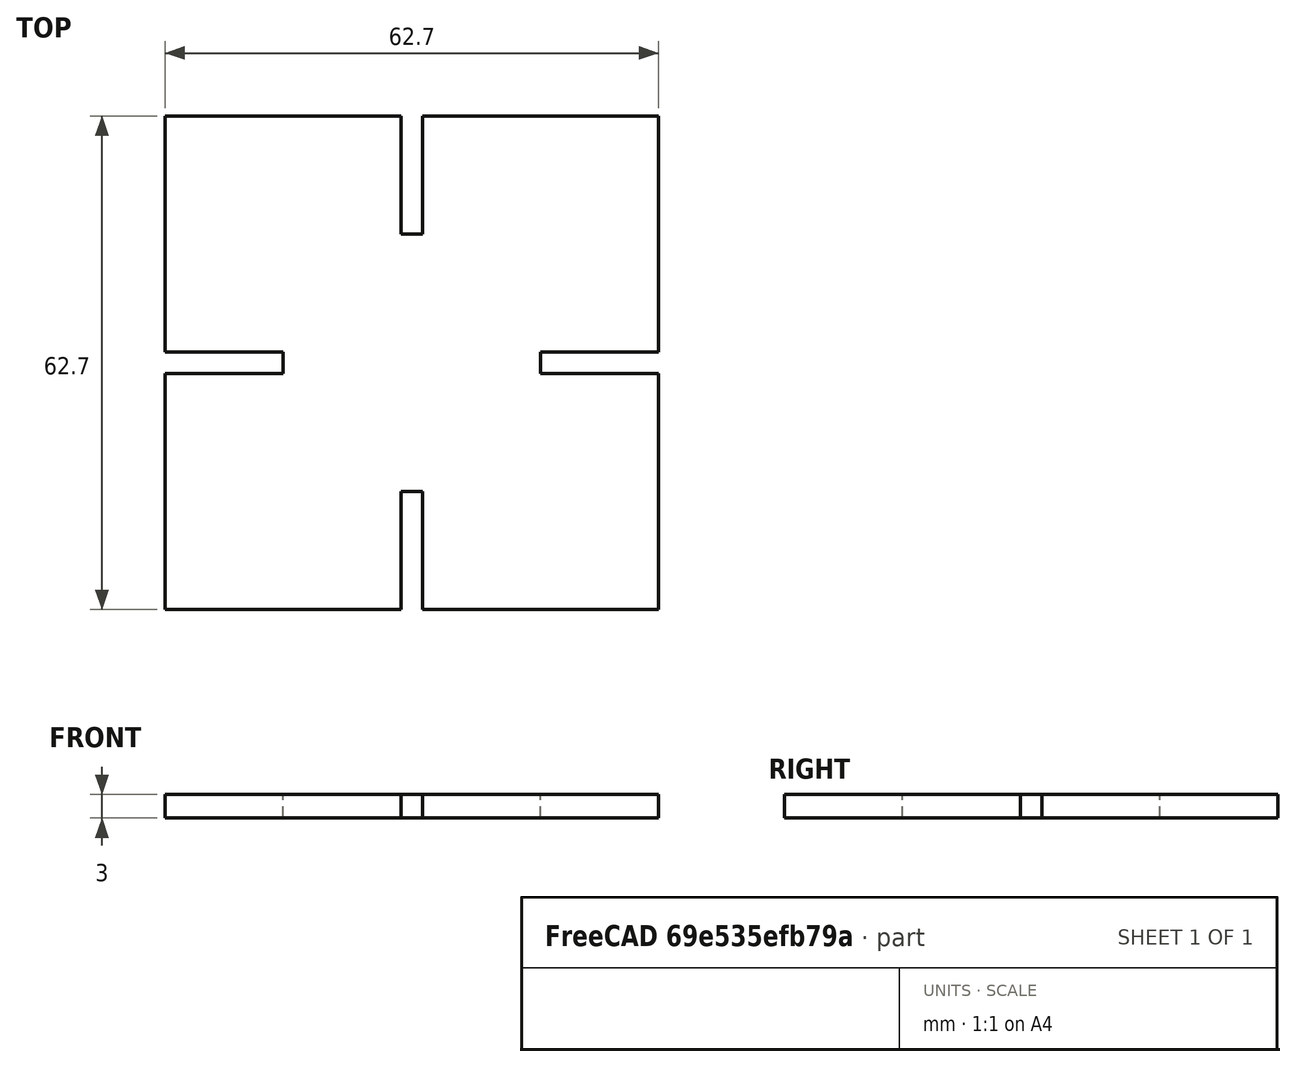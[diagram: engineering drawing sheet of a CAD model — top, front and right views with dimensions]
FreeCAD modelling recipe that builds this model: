
FCSTD DOCUMENT  (FreeCAD 0.19RUnknown)
Label: block
License: All rights reserved
LicenseURL: http://en.wikipedia.org/wiki/All_rights_reserved
objects: Sketcher::SketchObject×1, PartDesign::Pad×1, PartDesign::Body×1, Spreadsheet::Sheet×1, TechDraw::DrawSVGTemplate×1, TechDraw::DrawViewPart×1, TechDraw::DrawPage×1
note: 4 computed .brp shape members not serialized (recipe doc carries the construction recipe); baked Part::Feature solids carry a one-line shape summary decoded from their .brp

FEATURE [Sketcher::SketchObject] Sketch
  FullyConstrained = true
  MapMode = 5
  Support = -> [XY_Plane]
  expr: Constraints[43] = Spreadsheet.slotwidth
  sketch-geometry (20):
    g0: LineSegment StartX=1.35 StartY=31.35 StartZ=0 EndX=31.35 EndY=31.35 EndZ=0
    g1: LineSegment StartX=31.35 StartY=31.35 StartZ=0 EndX=31.35 EndY=1.35 EndZ=0
    g2: LineSegment StartX=31.35 StartY=1.35 StartZ=0 EndX=16.35 EndY=1.35 EndZ=0
    g3: LineSegment StartX=16.35 StartY=1.35 StartZ=0 EndX=16.35 EndY=-1.35 EndZ=0
    g4: LineSegment StartX=16.35 StartY=-1.35 StartZ=0 EndX=31.35 EndY=-1.35 EndZ=0
    g5: LineSegment StartX=31.35 StartY=-1.35 StartZ=0 EndX=31.35 EndY=-31.35 EndZ=0
    g6: LineSegment StartX=31.35 StartY=-31.35 StartZ=0 EndX=1.35 EndY=-31.35 EndZ=0
    g7: LineSegment StartX=1.35 StartY=-31.35 StartZ=0 EndX=1.35 EndY=-16.35 EndZ=0
    g8: LineSegment StartX=1.35 StartY=-16.35 StartZ=0 EndX=-1.35 EndY=-16.35 EndZ=0
    g9: LineSegment StartX=-1.35 StartY=-16.35 StartZ=0 EndX=-1.35 EndY=-31.35 EndZ=0
    g10: LineSegment StartX=-1.35 StartY=-31.35 StartZ=0 EndX=-31.35 EndY=-31.35 EndZ=0
    g11: LineSegment StartX=-31.35 StartY=-31.35 StartZ=0 EndX=-31.35 EndY=-1.35 EndZ=0
    g12: LineSegment StartX=-31.35 StartY=-1.35 StartZ=0 EndX=-16.35 EndY=-1.35 EndZ=0
    g13: LineSegment StartX=-16.35 StartY=-1.35 StartZ=0 EndX=-16.35 EndY=1.35 EndZ=0
    g14: LineSegment StartX=-16.35 StartY=1.35 StartZ=0 EndX=-31.35 EndY=1.35 EndZ=0
    g15: LineSegment StartX=-31.35 StartY=1.35 StartZ=0 EndX=-31.35 EndY=31.35 EndZ=0
    g16: LineSegment StartX=-31.35 StartY=31.35 StartZ=0 EndX=-1.35 EndY=31.35 EndZ=0
    g17: LineSegment StartX=-1.35 StartY=31.35 StartZ=0 EndX=-1.35 EndY=16.35 EndZ=0
    g18: LineSegment StartX=-1.35 StartY=16.35 StartZ=0 EndX=1.35 EndY=16.35 EndZ=0
    g19: LineSegment StartX=1.35 StartY=16.35 StartZ=0 EndX=1.35 EndY=31.35 EndZ=0
  constraints (59):
    c: Horizontal(g0)
    c: Coincident(g0,g1)
    c: Vertical(g1)
    c: Coincident(g1,g2)
    c: Horizontal(g2)
    c: Coincident(g2,g3)
    c: Vertical(g3)
    c: Coincident(g3,g4)
    c: Horizontal(g4)
    c: Coincident(g4,g5)
    c: Coincident(g5,g6)
    c: Coincident(g6,g7)
    c: Vertical(g7)
    c: Coincident(g7,g8)
    c: Coincident(g8,g9)
    c: Coincident(g9,g10)
    c: Horizontal(g10)
    c: Coincident(g10,g11)
    c: Vertical(g11)
    c: Coincident(g11,g12)
    c: Horizontal(g12)
    c: Coincident(g12,g13)
    c: Vertical(g13)
    c: Coincident(g13,g14)
    c: Horizontal(g14)
    c: Coincident(g14,g15)
    c: Vertical(g15)
    c: Coincident(g15,g16)
    c: Horizontal(g16)
    c: Coincident(g16,g17)
    c: Vertical(g17)
    c: Coincident(g17,g18)
    c: Horizontal(g18)
    c: Coincident(g18,g19)
    c: Vertical(g19)
    c: Coincident(g0,g19)
    c: Horizontal(g6)
    c: Horizontal(g8)
    c: Vertical(g9)
    c: Vertical(g5)
    c: Equal(g8,g3)
    c: Equal(g3,g18)
    c: Equal(g18,g13)
    c: Distance(g13) = 2.7
    c: Equal(g16,g15)
    c: Equal(g15,g11)
    c: Equal(g11,g10)
    c: Equal(g10,g6)
    c: Equal(g6,g5)
    c: Equal(g5,g1)
    c: Equal(g1,g0)
    c: Distance(g15) = 30
    c: Equal(g7,g9)
    c: Equal(g9,g4)
    c: Equal(g4,g2)
    c: Equal(g2,g19)
    c: Equal(g17,g14)
    c: Symmetric(g15,g5,g-1)
    c: Distance(g14) = 15
FEATURE [PartDesign::Pad] Pad
  Direction = (1,1,1)
  Length = 3
  Length2 = 100
  Profile = -> Sketch
  Refine = true
  Type = 0
FEATURE [PartDesign::Body] Body
  Group = -> [Sketch,Pad]
  Origin = -> Origin
  Tip = -> Pad
FEATURE [Spreadsheet::Sheet] Spreadsheet
  cells = A2=kerf; B2(kerf)=0.1; A3=slotwidth; B3(slotwidth)==thickness - kerf; A4=thickness; B4(thickness)=2.8
FEATURE [TechDraw::DrawSVGTemplate] Template
  EditableTexts = Designed_by_Name=Designed by Name; Drawing_number=Drawing number; FC-Date=Date; FC-SC=Scale; FC-SH=Sheet; FC-Title=Title; Subtitle=Subtitle; Weight=Weight
  Height = 210
  Orientation = 1
  Width = 297
FEATURE [TechDraw::DrawViewPart] View
  CoarseView = false
  Direction = (0,0,1)
  Focus = 100
  HardHidden = false
  IsoCount = 0
  IsoHidden = false
  IsoVisible = false
  LockPosition = false
  Perspective = false
  Rotation = 0
  ScaleType = 0
  SeamHidden = false
  SeamVisible = true
  SmoothHidden = false
  SmoothVisible = true
  Source = -> [Pad]
  X = 148.5
  XDirection = (1,0,0)
  Y = 105
FEATURE [TechDraw::DrawPage] Page
  KeepUpdated = true
  NextBalloonIndex = 1
  ProjectionType = 0
  Template = -> Template
  Views = -> [View]
